# Revit family: JOMA_Universalbeslag 100 & 130 Höger
name_source: partatom
category: Structural Connections
revit_build: Autodesk Revit Structure 2012 (Build: 20110309_2315(x64)
units: mm (PartAtom-declared; Revit-internal decimal feet)

## types (2) — shared parameters
Länk Joma Dimensioneringsverktyg = http://www.joma.se
Material = Varmförzinkad stålplåt
zero-valued in all types: Default Elevation

## per-type parameters (varying)
| type | Typ 100 | Typ 130 | Vikt | b | b2 | d | d2 | d3 | h | h2 | h3 | h4 |
| 8880100H | Yes | No | 0,15 | 59.5 mm | 49.1 mm | 51.84 mm  [stored 0.170079 ft] | 39.34 mm  [stored 0.129068 ft] | 2.5 mm  [stored 0.0082021 ft] | 100 mm  [stored 0.328084 ft] | 52 mm | 17.35 mm  [stored 0.0569226 ft] | 2.5 mm  [stored 0.0082021 ft] |
| 8880130H | No | Yes | 0,23 | 59 mm | 50 mm  [stored 0.164042 ft] | 60.34 mm  [stored 0.197966 ft] | 61.56 mm  [stored 0.201969 ft] | 10.06 mm  [stored 0.0330052 ft] | 130 mm  [stored 0.426509 ft] | 73.5 mm  [stored 0.241142 ft] | 21 mm  [stored 0.0688976 ft] | 10.3 mm |

note: [stored X ft] marks values corroborated as IEEE doubles in the binary element streams (Revit-internal decimal feet)

## geometry (parser evidence)
native form markers: Sweep x1
no freeform markers — native parametric forms only
